# Revit family: KOMFORT ERV EC DB
name_source: partatom
category: Оборудование
units: mm (PartAtom-declared; Revit-internal decimal feet)

## family parameters
Всегда вертикально = Да
Классификация = Нет
На основе рабочей плоскости = Нет
Общий = Нет
При загрузке вырезать с полостями = Нет
Размер круглого соединителя = Использовать диаметр
Тип детали = Нормальный
Точка принадлежности помещению = Нет

## types (21) — shared parameters
00_20_Manufacturer = Blauberg
00_20_Name = Heat and energy recovery air Handling unit
Casing Material = Steel, galvanized
Frequency = 50 Гц
L3 = 138 мм
L5 = 138 мм
Load Classification = HVAC
Maintenance zone material = <По категории>
Number of Fase = 1
Pressure_Static_Air = 0.0 Па
URL = https://blaubergventilatoren.de
Voltage = 230 В
a = 45 мм
w = 50 мм
Изготовитель = Blauberg
zero-valued in all types: Отметка по умолчанию

## per-type parameters (varying)
- KOMFORT ERV D 100 L S3: A=734 мм; A1=600 мм; Amperage=0 А; Apparent Load=76 В·А; B=481 мм; B1=571 мм; D=100 мм; Diameter=100 мм; Dy=95 мм; Filter=G4/G4 and F8 (PM2.5 93 %); H1=223 мм; Height=223 мм; L=300 мм; L1=92 мм; L11=91 мм; L2=128 мм; L22=91 мм; L33=113 мм; L4=113 мм; Length=734 мм; Maximum Air Flow=160.0 м³/ч; Power=76 Вт; Sound pressure level at 3 m distance=47 dBA; Temperature of moving air=-15...+40 °С; Weight=17.00 кг; Width=571 мм
- KOMFORT ERV D 200 L S3: A=987 мм; A1=854 мм; Amperage=1 А; Apparent Load=145 В·А; B=704 мм; B1=793 мм; D=150 мм; Diameter=150 мм; Dy=145 мм; Filter=G4/G4 and F8 (PM2.5 93 %); H1=241 мм; Height=241 мм; L=480 мм; L1=92 мм; L11=112 мм; L2=128 мм; L22=112 мм; L33=113 мм; L4=113 мм; Length=987 мм; Maximum Air Flow=280.0 м³/ч; Power=141 Вт; Sound pressure level at 3 m distance=49 dBA; Temperature of moving air=-15...+40 °С; Weight=24.00 кг; Width=793 мм
- KOMFORT ERV D 300 L S3: A=987 мм; A1=854 мм; Amperage=1 А; Apparent Load=193 В·А; B=704 мм; B1=793 мм; D=150 мм; Diameter=150 мм; Dy=145 мм; Filter=G4/G4 and F8 (PM2.5 93 %); H1=246 мм; Height=246 мм; L=480 мм; L1=92 мм; L11=112 мм; L2=128 мм; L22=112 мм; L33=113 мм; L4=113 мм; Length=987 мм; Maximum Air Flow=340.0 м³/ч; Power=193 Вт; Sound pressure level at 3 m distance=52 dBA; Temperature of moving air=-15...+40 °С; Weight=27.00 кг; Width=793 мм
- KOMFORT ERV D 450 L S3: A=1157 мм; A1=1024 мм; Amperage=2 А; Apparent Load=354 В·А; B=754 мм; B1=843 мм; D=150 мм; Diameter=150 мм; Dy=145 мм; Filter=G4/G4 and F8 (PM2.5 93 %); H1=296 мм; Height=296 мм; L=488 мм; L1=92 мм; L11=133 мм; L2=128 мм; L22=133 мм; L33=113 мм; L4=113 мм; Length=1157 мм; Maximum Air Flow=500.0 м³/ч; Power=354 Вт; Sound pressure level at 3 m distance=57 dBA; Temperature of moving air=-15...+40 °С; Weight=39.00 кг; Width=843 мм
- KOMFORT ERV D 150 L S3: A=947 мм; A1=854 мм; Amperage=1 А; Apparent Load=138 В·А; B=704 мм; B1=793 мм; D=99 мм; Diameter=99 мм; Dy=94 мм; Filter=G4/G4 and F8 (PM2.5 93 %); H1=247 мм; Height=247 мм; L=480 мм; L1=92 мм; L11=92 мм; L2=128 мм; L22=128 мм; L33=113 мм; L4=113 мм; Length=947 мм; Maximum Air Flow=230.0 м³/ч; Power=125 Вт; Sound pressure level at 3 m distance=49 dBA; Temperature of moving air=-15...+40 °С; Weight=26.00 кг; Width=793 мм
- KOMFORT ERV D 250 L S3: A=947 мм; A1=854 мм; Amperage=1 А; Apparent Load=253 В·А; B=704 мм; B1=793 мм; D=149 мм; Diameter=149 мм; Dy=144 мм; Filter=G4/G4 and F8 (PM2.5 83 %); H1=247 мм; Height=247 мм; L=480 мм; L1=92 мм; L11=92 мм; L2=128 мм; L22=128 мм; L33=113 мм; L4=113 мм; Length=947 мм; Maximum Air Flow=370.0 м³/ч; Power=250 Вт; Sound pressure level at 3 m distance=52 dBA; Temperature of moving air=-15...+40 °С; Weight=29.00 кг; Width=793 мм
- KOMFORT ERV D 350 L S3: A=1117 мм; A1=1024 мм; Amperage=1 А; Apparent Load=322 В·А; B=754 мм; B1=843 мм; D=149 мм; Diameter=149 мм; Dy=144 мм; Filter=G4/G4 and F8 (PM2.5 87 %); H1=297 мм; Height=297 мм; L=488 мм; L1=109 мм; L11=109 мм; L2=153 мм; L22=153 мм; L33=88 мм; L4=88 мм; Length=1117 мм; Maximum Air Flow=400.0 м³/ч; Power=310 Вт; Sound pressure level at 3 m distance=57 dBA; Temperature of moving air=-15...+40 °С; Weight=42.00 кг; Width=843 мм
- KOMFORT ERV D 100 R S3: A=734 мм; A1=600 мм; Amperage=0 А; Apparent Load=76 В·А; B=481 мм; B1=571 мм; D=100 мм; Diameter=100 мм; Dy=95 мм; Filter=G4/G4 and F8 (PM2.5 93 %); H1=223 мм; Height=223 мм; L=300 мм; L1=92 мм; L11=91 мм; L2=128 мм; L22=91 мм; L33=113 мм; L4=113 мм; Length=734 мм; Maximum Air Flow=160.0 м³/ч; Power=76 Вт; Sound pressure level at 3 m distance=47 dBA; Temperature of moving air=-15...+40 °С; Weight=17.00 кг; Width=571 мм
- KOMFORT ERV D 150 R S3: A=947 мм; A1=854 мм; Amperage=1 А; Apparent Load=138 В·А; B=704 мм; B1=793 мм; D=99 мм; Diameter=99 мм; Dy=94 мм; Filter=G4/G4 and F8 (PM2.5 93 %); H1=247 мм; Height=247 мм; L=480 мм; L1=92 мм; L11=92 мм; L2=128 мм; L22=128 мм; L33=113 мм; L4=113 мм; Length=947 мм; Maximum Air Flow=230.0 м³/ч; Power=125 Вт; Sound pressure level at 3 m distance=49 dBA; Temperature of moving air=-15...+40 °С; Weight=26.00 кг; Width=793 мм
- KOMFORT ERV D 200 R S3: A=987 мм; A1=854 мм; Amperage=1 А; Apparent Load=145 В·А; B=704 мм; B1=793 мм; D=150 мм; Diameter=150 мм; Dy=145 мм; Filter=G4/G4 and F8 (PM2.5 93 %); H1=241 мм; Height=241 мм; L=480 мм; L1=92 мм; L11=112 мм; L2=128 мм; L22=112 мм; L33=113 мм; L4=113 мм; Length=987 мм; Maximum Air Flow=280.0 м³/ч; Power=141 Вт; Sound pressure level at 3 m distance=49 dBA; Temperature of moving air=-15...+40 °С; Weight=24.00 кг; Width=793 мм
- KOMFORT ERV D 250 R S3: A=947 мм; A1=854 мм; Amperage=1 А; Apparent Load=253 В·А; B=704 мм; B1=793 мм; D=149 мм; Diameter=149 мм; Dy=144 мм; Filter=G4/G4 and F8 (PM2.5 83 %); H1=247 мм; Height=247 мм; L=480 мм; L1=92 мм; L11=92 мм; L2=128 мм; L22=128 мм; L33=113 мм; L4=113 мм; Length=947 мм; Maximum Air Flow=370.0 м³/ч; Power=250 Вт; Sound pressure level at 3 m distance=52 dBA; Temperature of moving air=-15...+40 °С; Weight=29.00 кг; Width=793 мм
- KOMFORT ERV D 300 R S3: A=987 мм; A1=854 мм; Amperage=1 А; Apparent Load=193 В·А; B=704 мм; B1=793 мм; D=150 мм; Diameter=150 мм; Dy=145 мм; Filter=G4/G4 and F8 (PM2.5 93 %); H1=246 мм; Height=246 мм; L=480 мм; L1=92 мм; L11=112 мм; L2=128 мм; L22=112 мм; L33=113 мм; L4=113 мм; Length=987 мм; Maximum Air Flow=340.0 м³/ч; Power=193 Вт; Sound pressure level at 3 m distance=52 dBA; Temperature of moving air=-15...+40 °С; Weight=27.00 кг; Width=793 мм
- KOMFORT ERV D 350 R S3: A=1117 мм; A1=1024 мм; Amperage=1 А; Apparent Load=322 В·А; B=754 мм; B1=843 мм; D=149 мм; Diameter=149 мм; Dy=144 мм; Filter=G4/G4 and F8 (PM2.5 87 %); H1=297 мм; Height=297 мм; L=488 мм; L1=109 мм; L11=109 мм; L2=153 мм; L22=153 мм; L33=88 мм; L4=88 мм; Length=1117 мм; Maximum Air Flow=400.0 м³/ч; Power=310 Вт; Sound pressure level at 3 m distance=57 dBA; Temperature of moving air=-15...+40 °С; Weight=42.00 кг; Width=843 мм
- KOMFORT ERV D 450 R S3: A=1157 мм; A1=1024 мм; Amperage=2 А; Apparent Load=354 В·А; B=754 мм; B1=843 мм; D=150 мм; Diameter=150 мм; Dy=145 мм; Filter=G4/G4 and F8 (PM2.5 93 %); H1=296 мм; Height=296 мм; L=488 мм; L1=92 мм; L11=133 мм; L2=128 мм; L22=133 мм; L33=113 мм; L4=113 мм; Length=1157 мм; Maximum Air Flow=500.0 м³/ч; Power=354 Вт; Sound pressure level at 3 m distance=57 dBA; Temperature of moving air=-15...+40 °С; Weight=39.00 кг; Width=843 мм
- KOMFORT ERV EC DB 100 L S14: A=734 мм; A1=600 мм; Amperage=1 А; Apparent Load=115 В·А; B=481 мм; B1=571 мм; D=100 мм; Diameter=100 мм; Dy=95 мм; Filter=G4/G4 and F8 (PM2.5 93 %); H1=229 мм; Height=229 мм; L=300 мм; L1=92 мм; L11=91 мм; L2=128 мм; L22=91 мм; L33=113 мм; L4=113 мм; Length=734 мм; Maximum Air Flow=170.0 м³/ч; Power=66 Вт; Sound pressure level at 3 m distance=30 dBA; Temperature of moving air=-25...+40 °С; Weight=17.00 кг; Width=571 мм
- KOMFORT ERV EC DB 150 L S14: A=987 мм; A1=854 мм; Amperage=1 А; Apparent Load=161 В·А; B=704 мм; B1=793 мм; D=100 мм; Diameter=100 мм; Dy=95 мм; Filter=G4/G4 and F8 (PM2.5 93 %); H1=241 мм; Height=241 мм; L=480 мм; L1=92 мм; L11=112 мм; L2=128 мм; L22=112 мм; L33=113 мм; L4=113 мм; Length=987 мм; Maximum Air Flow=215.0 м³/ч; Power=83 Вт; Sound pressure level at 3 m distance=32 dBA; Temperature of moving air=-25...+40 °С; Weight=26.00 кг; Width=793 мм
- KOMFORT ERV EC DB 150 R S14: A=987 мм; A1=854 мм; Amperage=1 А; Apparent Load=161 В·А; B=704 мм; B1=793 мм; D=100 мм; Diameter=100 мм; Dy=95 мм; Filter=G4/G4 and F8 (PM2.5 93 %); H1=241 мм; Height=241 мм; L=480 мм; L1=92 мм; L11=112 мм; L2=128 мм; L22=112 мм; L33=113 мм; L4=113 мм; Length=987 мм; Maximum Air Flow=215.0 м³/ч; Power=83 Вт; Sound pressure level at 3 m distance=32 dBA; Temperature of moving air=-25...+40 °С; Weight=26.00 кг; Width=793 мм
- KOMFORT ERV EC DB 250 L S14: A=987 мм; A1=854 мм; Amperage=1 А; Apparent Load=161 В·А; B=704 мм; B1=793 мм; D=150 мм; Diameter=150 мм; Dy=145 мм; Filter=G4/G4 and F8 (PM2.5 93 %); H1=246 мм; Height=246 мм; L=480 мм; L1=92 мм; L11=112 мм; L2=128 мм; L22=112 мм; L33=113 мм; L4=113 мм; Length=987 мм; Maximum Air Flow=300.0 м³/ч; Power=84 Вт; Sound pressure level at 3 m distance=36 dBA; Temperature of moving air=-25...+40 °С; Weight=29.00 кг; Width=793 мм
- KOMFORT ERV EC DB 250 R S14: A=987 мм; A1=854 мм; Amperage=1 А; Apparent Load=161 В·А; B=704 мм; B1=793 мм; D=150 мм; Diameter=150 мм; Dy=145 мм; Filter=G4/G4 and F8 (PM2.5 93 %); H1=246 мм; Height=246 мм; L=480 мм; L1=92 мм; L11=112 мм; L2=128 мм; L22=112 мм; L33=113 мм; L4=113 мм; Length=987 мм; Maximum Air Flow=300.0 м³/ч; Power=84 Вт; Sound pressure level at 3 m distance=36 dBA; Temperature of moving air=-25...+40 °С; Weight=29.00 кг; Width=793 мм
- KOMFORT ERV EC DB 350 L S14: A=1157 мм; A1=1024 мм; Amperage=1 А; Apparent Load=299 В·А; B=754 мм; B1=843 мм; D=150 мм; Diameter=150 мм; Dy=145 мм; Filter=G4/G4 and F8 (PM2.5 93 %); H1=296 мм; Height=296 мм; L=488 мм; L1=109 мм; L11=133 мм; L2=153 мм; L22=133 мм; L33=88 мм; L4=88 мм; Length=1157 мм; Maximum Air Flow=430.0 м³/ч; Power=171 Вт; Sound pressure level at 3 m distance=46 dBA; Temperature of moving air=-25...+40 °С; Weight=42.00 кг; Width=843 мм
- KOMFORT ERV EC DB 350 R S14: A=1157 мм; A1=1024 мм; Amperage=1 А; Apparent Load=299 В·А; B=754 мм; B1=843 мм; D=150 мм; Diameter=150 мм; Dy=145 мм; Filter=G4/G4 and F8 (PM2.5 93 %); H1=296 мм; Height=296 мм; L=488 мм; L1=109 мм; L11=133 мм; L2=153 мм; L22=133 мм; L33=88 мм; L4=88 мм; Length=1157 мм; Maximum Air Flow=430.0 м³/ч; Power=171 Вт; Sound pressure level at 3 m distance=46 dBA; Temperature of moving air=-25...+40 °С; Weight=42.00 кг; Width=843 мм

note: column(s) folded — value = type name in every type: 00_20_Type
